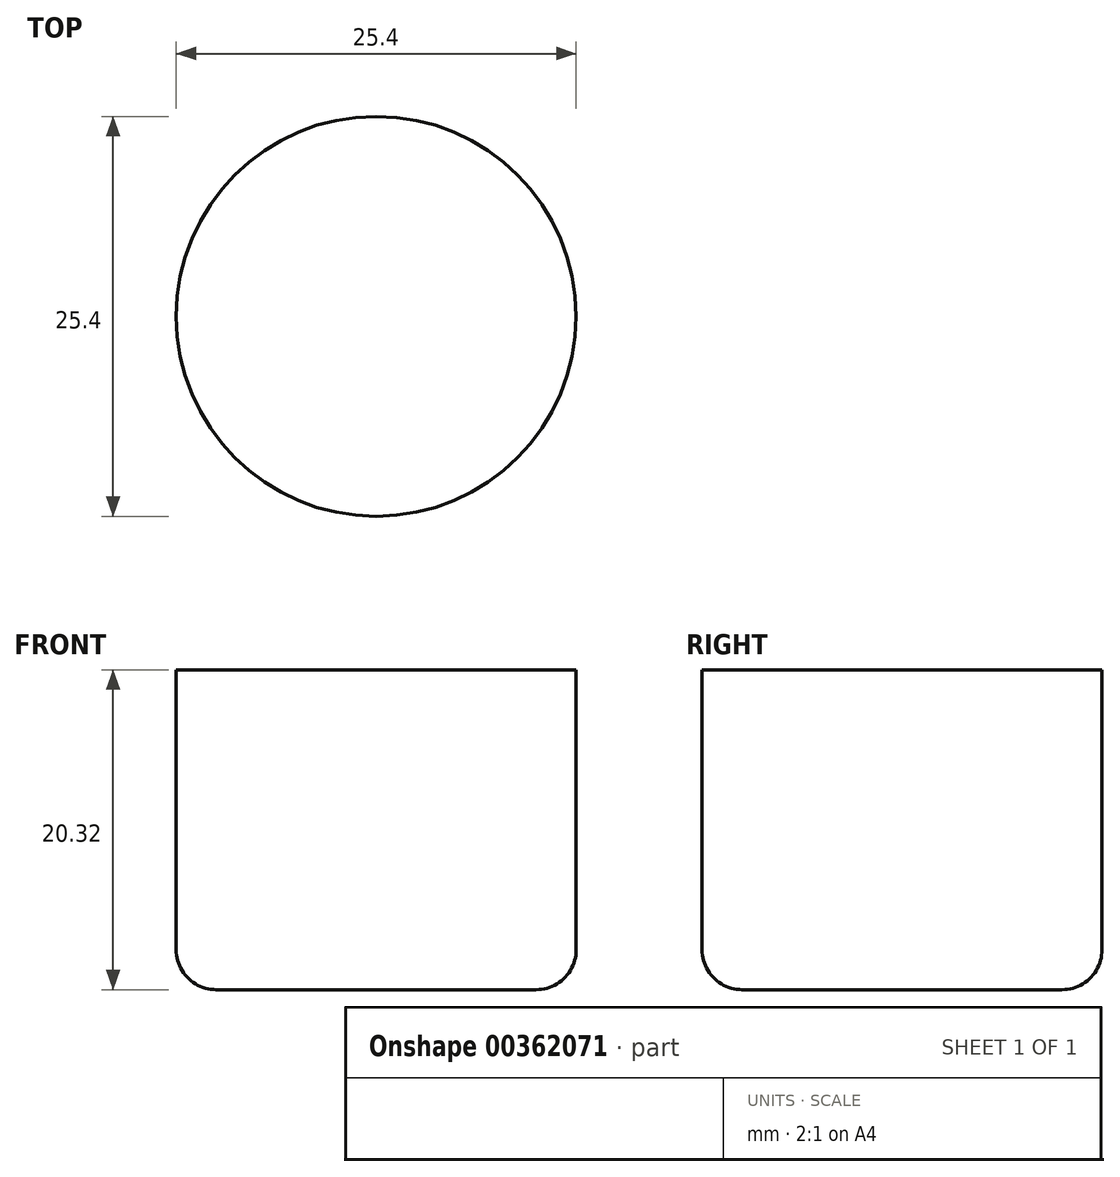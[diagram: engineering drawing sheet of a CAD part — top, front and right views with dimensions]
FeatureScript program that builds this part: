
annotation { "Feature Type Name" : "Feature", "Feature Type Description" : "" }
export const myFeature = defineFeature(function(context is Context, id is Id, definition is map)
    precondition{}
    {
        {
            var Q0;
            Q0=qCreatedBy(makeId("Front.planeOp"),FACE);
            var sketch = newSketch(context, id + "F0", { "sketchPlane" : qUnion([Q0])});
            skLineSegment(sketch, "E0", {"start": v(0, -45.74) * mm, "end": v(-12.7, -45.74) * mm});
            skLineSegment(sketch, "E1", {"start": v(-12.7, -45.74) * mm, "end": v(-12.7, -25.42) * mm});
            skLineSegment(sketch, "E2", {"start": v(-12.7, -25.42) * mm, "end": v(0, -25.42) * mm});
            skLineSegment(sketch, "E3", {"start": v(0, -25.42) * mm, "end": v(0, -45.74) * mm});
            skSolve(sketch);
        }
        {
            var Q0;
            Q0=makeQuery(id+"F0.imprint","IMPRINT",FACE,{"disambiguationData":[TD([[makeQuery(id+"F0.imprint","IMPRINT",EDGE,{"derivedFrom":sQuery(id+"F0.wireOp",EDGE,"E0")}),-1.0]])]});
            var Q1;
            Q1=sQuery(id+"F0.wireOp",EDGE,"E3");
            revolve(context, id + "F1", {"entities" : qUnion([Q0]), "axis" : qUnion([Q1]), "revolveType" : RevolveType.FULL});
        }
        {
            var Q0;
            Q0=makeQuery(id+"F1.opRevolve","SWEPT_EDGE",EDGE,{"disambiguationData":[OSD([sQuery(id+"F0.wireOp",EDGE,"E0"),sQuery(id+"F0.wireOp",EDGE,"E1")])]});
            fillet(context, id + "F2", {"entities" : qUnion([Q0]), "radius" : 2.54 * mm, "tangentPropagation" : true, "allowEdgeOverflow" : false});
        }
    });
